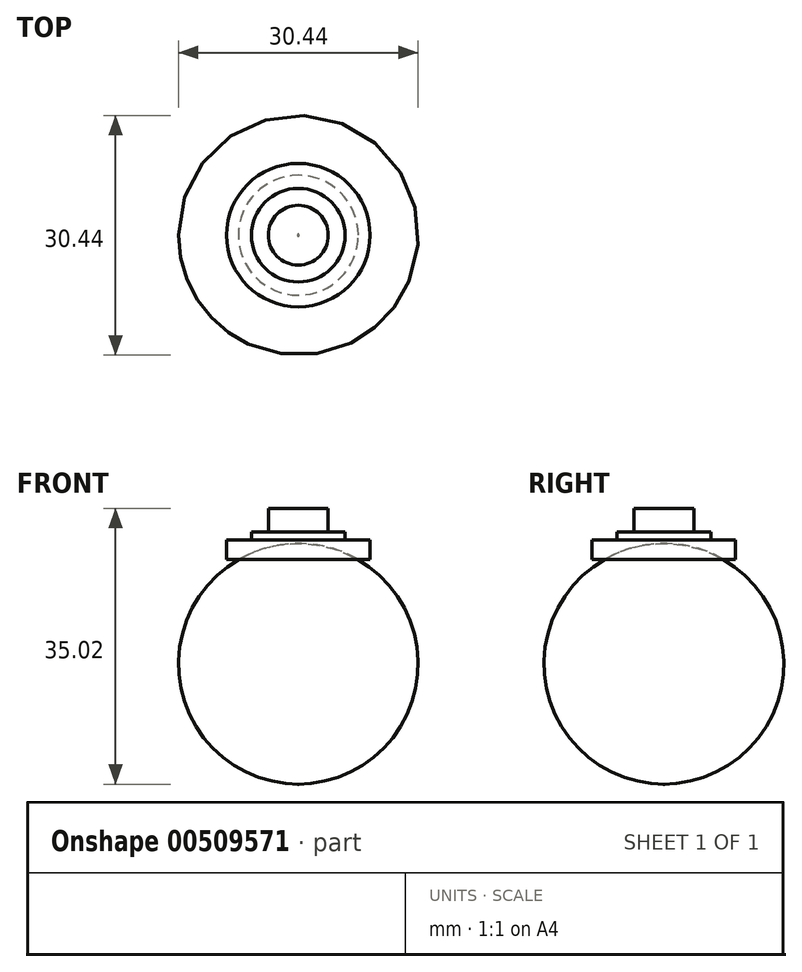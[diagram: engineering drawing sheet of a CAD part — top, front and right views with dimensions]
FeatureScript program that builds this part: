
annotation { "Feature Type Name" : "Feature", "Feature Type Description" : "" }
export const myFeature = defineFeature(function(context is Context, id is Id, definition is map)
    precondition{}
    {
        {
            var Q0;
            Q0=qCreatedBy(makeId("Right.planeOp"),FACE);
            var sketch = newSketch(context, id + "F0", { "sketchPlane" : qUnion([Q0])});
            skArc(sketch, "E0", {"start": v(7.62, 0) * mm, "mid": v(3.94, 1.5) * mm, "end": v(0, 2) * mm});
            skLineSegment(sketch, "E1", {"start": v(7.62, 0) * mm, "end": v(9.12, 0) * mm});
            skPoint(sketch, "E2.endSnap0", {"position": v(0.06, 2) * mm});
            skLineSegment(sketch, "E3", {"start": v(0, 2) * mm, "end": v(0, 6.46) * mm});
            skLineSegment(sketch, "E4", {"start": v(0, 6.46) * mm, "end": v(3.8, 6.46) * mm});
            skLineSegment(sketch, "E5", {"start": v(3.8, 6.46) * mm, "end": v(3.8, 3.46) * mm});
            skLineSegment(sketch, "E6", {"start": v(3.8, 3.46) * mm, "end": v(5.95, 3.46) * mm});
            skLineSegment(sketch, "E7", {"start": v(5.95, 3.46) * mm, "end": v(5.95, 2.46) * mm});
            skLineSegment(sketch, "E8", {"start": v(5.95, 2.46) * mm, "end": v(9.12, 2.46) * mm});
            skLineSegment(sketch, "E9", {"start": v(9.12, 2.46) * mm, "end": v(9.12, 0) * mm});
            skLineSegment(sketch, "E10", {"start": v(0, 6.46) * mm, "end": v(0, 0) * mm});
            skSolve(sketch);
        }
        {
            var Q0;
            {var subQ1=sQuery(id+"F0.wireOp",EDGE,"E0");Q0=makeQuery(id+"F0.imprint","IMPRINT",FACE,{"disambiguationData":[TD([[makeQuery(id+"F0.imprint","IMPRINT",EDGE,{"derivedFrom":subQ1}),-1.0]])]});}
            var Q1;
            Q1=sQuery(id+"F0.wireOp",EDGE,"E10");
            revolve(context, id + "F1", {"entities" : qUnion([Q0]), "axis" : qUnion([Q1]), "revolveType" : RevolveType.FULL});
        }
    });
